# Revit family: Ribbeelement - RTPA Rampe
name_source: partatom
category: Structural Framing
units: mm (PartAtom-declared; Revit-internal decimal feet)

## family parameters
Always export as geometry = No
Always vertical = Yes
Cut with Voids When Loaded = No
Material for Model Behavior = Other
OmniClass Number = 23.25.30.11.14.14
OmniClass Title = Beams
Section Shape = Not Defined
Shared = No
Show family pre-cut in plan views = Yes

## types (1)
- Ribbeelement - RTPA Rampe
    -------------------- NIX PILLE! ------------------- = Parametre heruder må ikke redigeres!
    -------------------- NIX PILLE! -------------------- = Parametre heruder må ikke redigeres!
    -------------------- NIX PILLE! --------------------- = Parametre heruder må ikke redigeres!
    Manufacturer = CRH Concrete
    Model = RTPA Rampe
    Structural Material = <By Category>
    Type_Kant_Reces_1 = xNested - Kantreces
    Type_Kant_Reces_2 = xNested - Kantreces NON
    _Højde Kip Standard = 560 mm  [stored 1.83727 ft]
    _Plade Hældning = 0.025
    _Plade Tykkelse Standard = 120 mm  [stored 0.393701 ft]
    _Plade Vinkel = 1.43°
    _Ribbe Bredde Bund = 137.6 mm
    _Ribbe Center Offset = 600 mm

note: [stored X ft] marks values corroborated as IEEE doubles in the binary element streams (Revit-internal decimal feet)

## geometry (parser evidence)
native form markers: Blend x41, Sweep x14
no freeform markers — native parametric forms only
